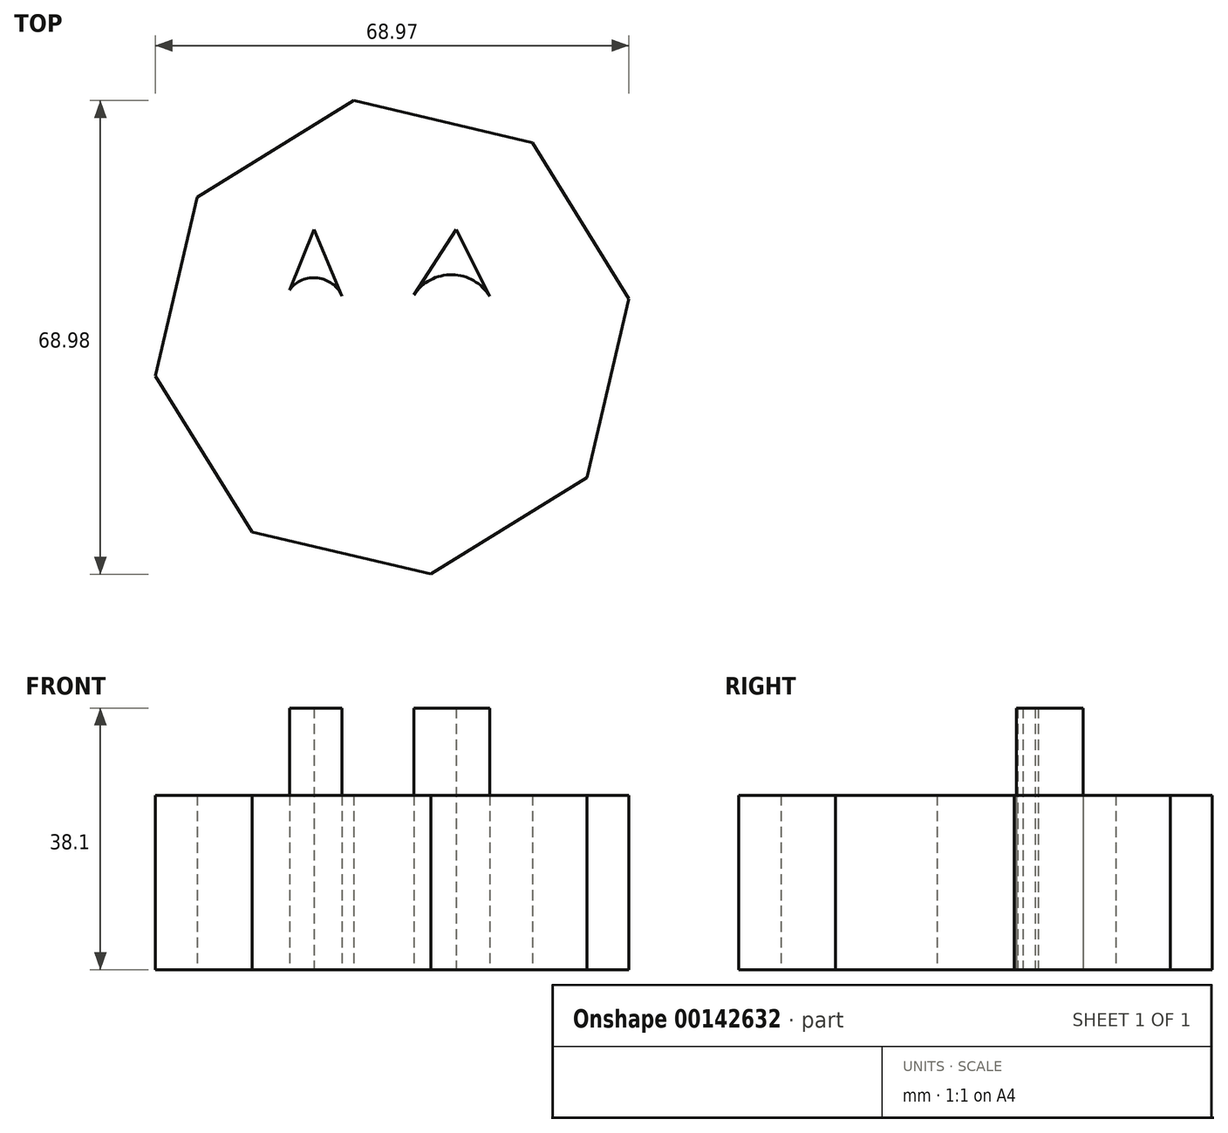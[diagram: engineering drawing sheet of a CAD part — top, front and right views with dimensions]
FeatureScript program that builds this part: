
annotation { "Feature Type Name" : "Feature", "Feature Type Description" : "" }
export const myFeature = defineFeature(function(context is Context, id is Id, definition is map)
    precondition{}
    {
        {
            var Q0;
            Q0=qCreatedBy(makeId("Top.planeOp"),FACE);
            var sketch = newSketch(context, id + "F0", { "sketchPlane" : qUnion([Q0])});
            skCircle(sketch, "E0.cCircle", {"center": v(-7.38, 11.67) * mm, "radius": 32.28 * mm, "construction": true});
            skLineSegment(sketch, "E0.0", {"start": v(20.99, -8.74) * mm, "end": v(-1.75, -22.82) * mm});
            skLineSegment(sketch, "E0.1", {"start": v(-1.75, -22.82) * mm, "end": v(-27.79, -16.7) * mm});
            skLineSegment(sketch, "E0.2", {"start": v(-27.79, -16.7) * mm, "end": v(-41.86, 6.05) * mm});
            skLineSegment(sketch, "E0.3", {"start": v(-41.86, 6.05) * mm, "end": v(-35.74, 32.08) * mm});
            skLineSegment(sketch, "E0.4", {"start": v(-35.74, 32.08) * mm, "end": v(-13, 46.16) * mm});
            skLineSegment(sketch, "E0.5", {"start": v(-13, 46.16) * mm, "end": v(13.03, 40.03) * mm});
            skLineSegment(sketch, "E0.6", {"start": v(13.03, 40.03) * mm, "end": v(27.11, 17.3) * mm});
            skLineSegment(sketch, "E0.7", {"start": v(27.11, 17.3) * mm, "end": v(20.99, -8.74) * mm});
            skPoint(sketch, "E0.0.midPoint", {"position": v(9.62, -15.78) * mm});
            skSolve(sketch);
        }
        {
            var Q0;
            Q0=qCreatedBy(makeId("Top.planeOp"),FACE);
            var sketch = newSketch(context, id + "F1", { "sketchPlane" : qUnion([Q0])});
            skLineSegment(sketch, "E1", {"start": v(-22.31, 18.58) * mm, "end": v(-18.77, 27.35) * mm});
            skLineSegment(sketch, "E2", {"start": v(-14.66, 17.65) * mm, "end": v(-18.77, 27.35) * mm});
            skLineSegment(sketch, "E3", {"start": v(-4.2, 17.83) * mm, "end": v(1.96, 27.35) * mm});
            skLineSegment(sketch, "E4", {"start": v(1.96, 27.35) * mm, "end": v(6.82, 17.65) * mm});
            skArc(sketch, "E5", {"start": v(-14.66, 17.65) * mm, "mid": v(-18.22, 20.33) * mm, "end": v(-22.31, 18.58) * mm});
            skArc(sketch, "E6", {"start": v(6.82, 17.65) * mm, "mid": v(1.36, 20.8) * mm, "end": v(-4.2, 17.83) * mm});
            skSolve(sketch);
        }
        {
            var Q0;
            Q0 = qSketchRegion(id + "F1", true);
            extrude(context, id + "F2", {"entities" : qUnion([Q0]), "depth" : 38.1 * mm});
        }
        {
            var Q0;
            Q0 = qSketchRegion(id + "F0", true);
            var Q1;
            Q1=makeQuery(id+"F0.imprint","IMPRINT",FACE,{"disambiguationData":[TD([[makeQuery(id+"F0.imprint","IMPRINT",EDGE,{"derivedFrom":sQuery(id+"F0.wireOp",EDGE,"E0.0")}),-1.0]])]});
            extrude(context, id + "F3", {"entities" : qUnion([Q0, Q1]), "depth" : 25.4 * mm});
        }
    });
